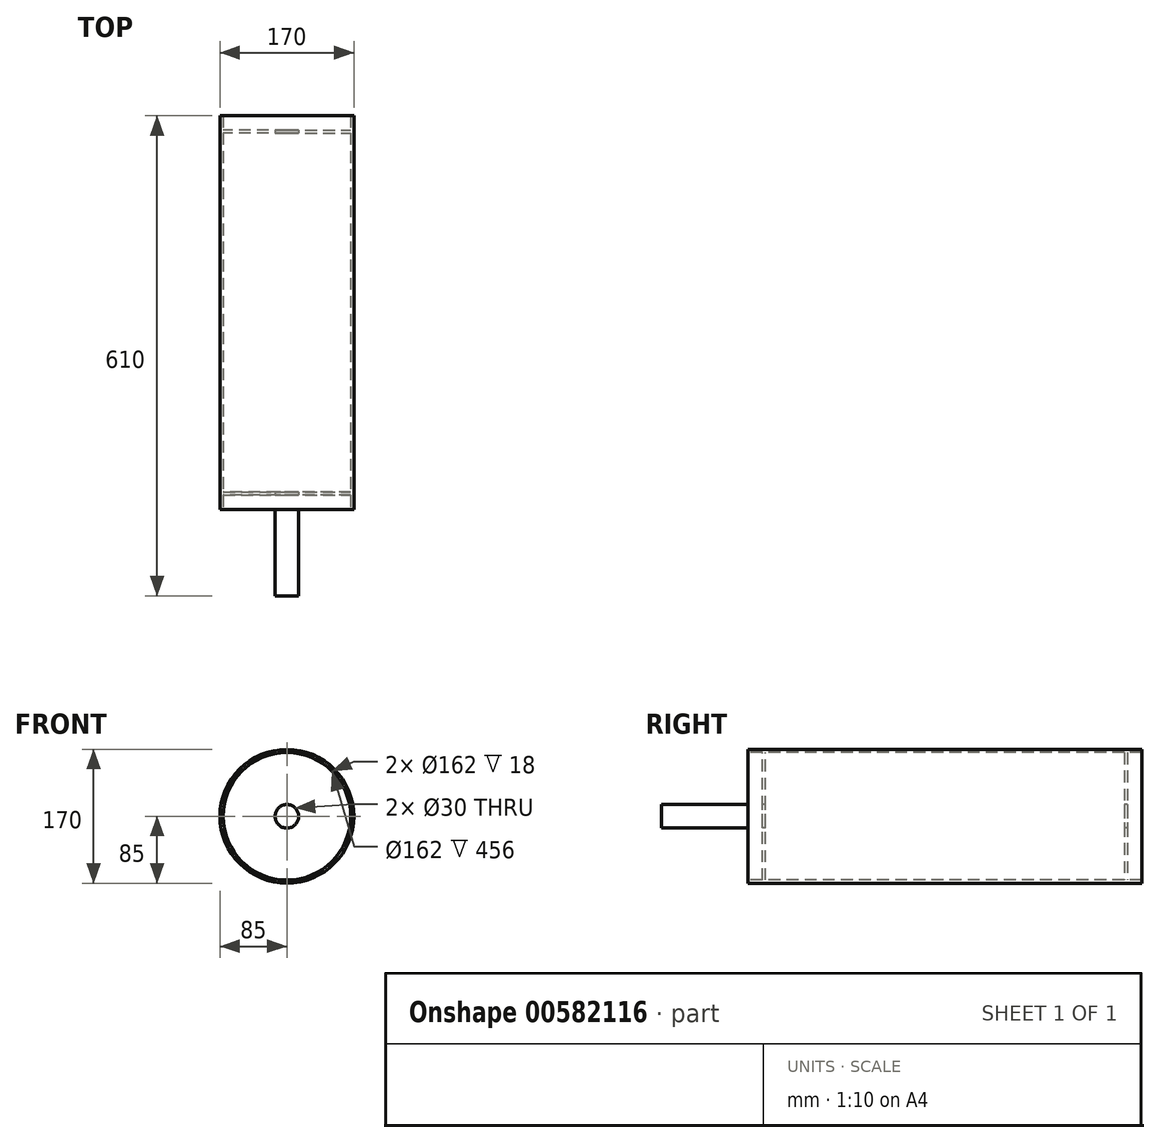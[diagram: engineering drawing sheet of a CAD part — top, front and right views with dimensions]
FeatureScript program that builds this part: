
annotation { "Feature Type Name" : "Feature", "Feature Type Description" : "" }
export const myFeature = defineFeature(function(context is Context, id is Id, definition is map)
    precondition{}
    {
        {
            var Q0;
            Q0=qCreatedBy(makeId("Front.planeOp"),FACE);
            var sketch = newSketch(context, id + "F0", { "sketchPlane" : qUnion([Q0])});
            skCircle(sketch, "E0", {"center": v(0, 0) * mm, "radius": 15 * mm});
            skSolve(sketch);
        }
        {
            var Q0;
            Q0=makeQuery(id+"F0.imprint","IMPRINT",FACE,{"disambiguationData":[TD([[makeQuery(id+"F0.imprint","IMPRINT",EDGE,{"derivedFrom":sQuery(id+"F0.wireOp",EDGE,"E0")}),1.0]])]});
            extrude(context, id + "F1", {"entities" : qUnion([Q0]), "depth" : 360 * mm, "offsetDistance" : 25 * mm, "hasSecondDirection" : true, "secondDirectionOppositeDirection" : true, "secondDirectionDepth" : 360 * mm});
        }
        {
            var Q0;
            Q0=qCreatedBy(makeId("Front.planeOp"),FACE);
            var sketch = newSketch(context, id + "F2", { "sketchPlane" : qUnion([Q0])});
            skCircle(sketch, "E1", {"center": v(0, 0) * mm, "radius": 85 * mm});
            skSolve(sketch);
        }
        {
            var Q0;
            Q0=makeQuery(id+"F2.imprint","IMPRINT",FACE,{"disambiguationData":[TD([[makeQuery(id+"F2.imprint","IMPRINT",EDGE,{"derivedFrom":sQuery(id+"F2.wireOp",EDGE,"E1")}),1.0]])]});
            extrude(context, id + "F3", {"entities" : qUnion([Q0]), "depth" : 250 * mm, "offsetDistance" : 25 * mm, "hasSecondDirection" : true, "secondDirectionOppositeDirection" : true, "secondDirectionDepth" : 250 * mm});
        }
        {
            var Q0;
            Q0=makeQuery(id+"F3.opExtrude","CAP_FACE",FACE,{"disambiguationData":[OSD([sQuery(id+"F2.wireOp",EDGE,"E1")])],"isStart":false});
            var sketch = newSketch(context, id + "F4", { "sketchPlane" : qUnion([Q0])});
            skCircle(sketch, "E2", {"center": v(0, 0) * mm, "radius": 81 * mm});
            skSolve(sketch);
        }
        {
            var Q0;
            Q0 = qSketchRegion(id + "F4", true);
            extrude(context, id + "F5", {"entities" : qUnion([Q0]), "operationType" : NewBodyOperationType.REMOVE, "endBound" : BoundingType.THROUGH_ALL, "oppositeDirection" : true, "depth" : 25 * mm, "offsetDistance" : 25 * mm});
        }
        {
            var Q0;
            Q0=makeQuery(id+"F3.opExtrude","CAP_FACE",FACE,{"disambiguationData":[OSD([sQuery(id+"F2.wireOp",EDGE,"E1")])],"isStart":false});
            cPlane(context, id + "F6", {"entities" : qUnion([Q0]), "cplaneType" : CPlaneType.OFFSET, "offset" : 20 * mm, "oppositeDirection" : true, "width" : 150 * mm, "height" : 150 * mm});
        }
        {
            var Q0;
            Q0=qCreatedBy(id+"F6.planeOp",FACE);
            var sketch = newSketch(context, id + "F7", { "sketchPlane" : qUnion([Q0])});
            skCircle(sketch, "E3", {"center": v(0, 0) * mm, "radius": 81 * mm});
            skSolve(sketch);
        }
        {
            var Q0;
            Q0 = qSketchRegion(id + "F7", true);
            extrude(context, id + "F8", {"entities" : qUnion([Q0]), "operationType" : NewBodyOperationType.ADD, "depth" : 2 * mm, "offsetDistance" : 25 * mm, "hasSecondDirection" : true, "secondDirectionOppositeDirection" : true, "secondDirectionDepth" : 2 * mm});
        }
        {
            var Q0;
            Q0=qCreatedBy(id+"F6.planeOp",FACE);
            var sketch = newSketch(context, id + "F9", { "sketchPlane" : qUnion([Q0])});
            skCircle(sketch, "E4", {"center": v(0, 0) * mm, "radius": 15 * mm});
            skSolve(sketch);
        }
        {
            var Q0;
            Q0 = qSketchRegion(id + "F9", true);
            extrude(context, id + "F10", {"entities" : qUnion([Q0]), "operationType" : NewBodyOperationType.REMOVE, "oppositeDirection" : true, "depth" : 4 * mm, "offsetDistance" : 25 * mm, "hasSecondDirection" : true, "secondDirectionOppositeDirection" : false, "secondDirectionDepth" : 4 * mm});
        }
        {
            var Q0;
            Q0=makeQuery(id+"F3.opExtrude","CAP_FACE",FACE,{"disambiguationData":[OSD([sQuery(id+"F2.wireOp",EDGE,"E1")])],"isStart":true});
            cPlane(context, id + "F11", {"entities" : qUnion([Q0]), "cplaneType" : CPlaneType.OFFSET, "offset" : 20 * mm, "oppositeDirection" : true, "width" : 150 * mm, "height" : 150 * mm});
        }
        {
            var Q0;
            Q0=qCreatedBy(id+"F11.planeOp",FACE);
            var sketch = newSketch(context, id + "F12", { "sketchPlane" : qUnion([Q0])});
            skCircle(sketch, "E5", {"center": v(0, 0) * mm, "radius": 81 * mm});
            skSolve(sketch);
        }
        {
            var Q0;
            Q0 = qSketchRegion(id + "F12", true);
            extrude(context, id + "F13", {"entities" : qUnion([Q0]), "operationType" : NewBodyOperationType.ADD, "depth" : 2 * mm, "offsetDistance" : 25 * mm, "hasSecondDirection" : true, "secondDirectionOppositeDirection" : true, "secondDirectionDepth" : 2 * mm});
        }
        {
            var Q0;
            Q0=qCreatedBy(id+"F11.planeOp",FACE);
            var sketch = newSketch(context, id + "F14", { "sketchPlane" : qUnion([Q0])});
            skCircle(sketch, "E6", {"center": v(0, 0) * mm, "radius": 15 * mm});
            skSolve(sketch);
        }
        {
            var Q0;
            Q0 = qSketchRegion(id + "F14", true);
            extrude(context, id + "F15", {"entities" : qUnion([Q0]), "operationType" : NewBodyOperationType.REMOVE, "depth" : 25 * mm, "offsetDistance" : 25 * mm, "hasSecondDirection" : true, "secondDirectionOppositeDirection" : true, "secondDirectionDepth" : 25 * mm});
        }
    });
